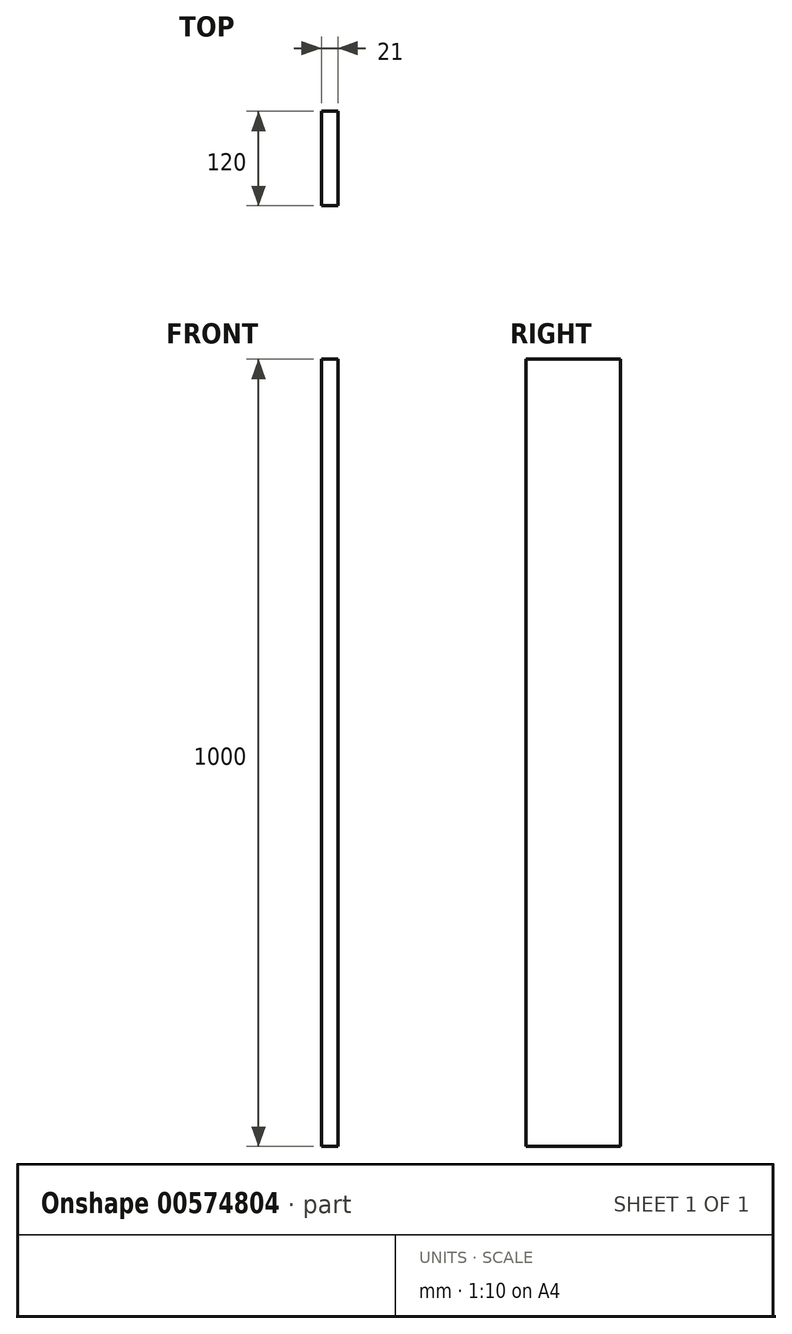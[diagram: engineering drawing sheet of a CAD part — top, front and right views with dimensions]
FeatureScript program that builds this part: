
annotation { "Feature Type Name" : "Feature", "Feature Type Description" : "" }
export const myFeature = defineFeature(function(context is Context, id is Id, definition is map)
    precondition{}
    {
        {
            var Q0;
            Q0=qCreatedBy(makeId("Top.planeOp"),FACE);
            var sketch = newSketch(context, id + "F0", { "sketchPlane" : qUnion([Q0])});
            skLineSegment(sketch, "E0.bottom", {"start": v(-10.5, 60) * mm, "end": v(10.5, 60) * mm});
            skLineSegment(sketch, "E0.top", {"start": v(-10.5, -60) * mm, "end": v(10.5, -60) * mm});
            skLineSegment(sketch, "E0.left", {"start": v(-10.5, 60) * mm, "end": v(-10.5, -60) * mm});
            skLineSegment(sketch, "E0.right", {"start": v(10.5, 60) * mm, "end": v(10.5, -60) * mm});
            skSolve(sketch);
        }
        {
            var Q0;
            Q0 = qSketchRegion(id + "F0", true);
            extrude(context, id + "F1", {"entities" : qUnion([Q0]), "depth" : 1000 * mm, "offsetDistance" : 25 * mm});
        }
    });
